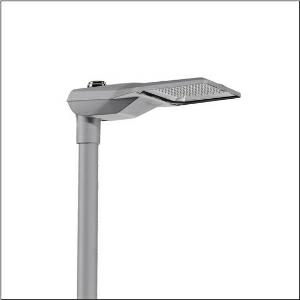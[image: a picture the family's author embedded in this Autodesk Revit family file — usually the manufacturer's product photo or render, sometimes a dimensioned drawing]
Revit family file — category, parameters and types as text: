
# Revit family: streetlight_sl_21_midi___st0_8a_5xe7c47n08lb_a78e
name_source: partatom
category: Lighting Fixtures
units: mm (PartAtom-declared; Revit-internal decimal feet)

## family parameters
Cut with Voids When Loaded = No
Host = Face
Light Source = No
Part Type = Normal
Room Calculation Point = No
Round Connector Dimension = Use Diameter
Shared = No

## types (1)
- --- (1 x LED, 14950 lm, 98.3 W, 4000K)
    Apparent Load = 98 VA
    CIE Flux Codes = 38 75 97 100 100
    Color Rendering = 70
    Color Temperature = 4000K
    Default Elevation = 1800 mm
    Description = Streetlight SL 21 midi, mast luminaire, primary light control with lens, of PMMA, primary optical cover: cover, of toughened safety glass, transparent, light distribution: ST0.8a, light emission: direct distribution, primary light characteristic: asymmetric, installation type: side-entry, LED, 3G 2.5mm², High Power LED, rated luminous flux: 14.950lm, luminous efficacy: 152lm/W, light colour: 740, colour temperature: 4000K, control gear: NEMA (7pin), control: overheat protection, pre-setting: linear dimming characteristic, constant luminous flux control, time-dependent luminous flux control, flexible luminous flux parameterisation, mains connection: 220..240V, AC, 50/60Hz, connection cable pre-assembled, cable length: 10,5m, wiring characteristics: H05VV-F, start of lifetime: 98W, end of service life: 101W, reduction: 45W, luminaire housing, of diecast aluminium (EN AC-44300), powder-coated, SITECO metallic grey (DB 702S), corrosivity category C5 high according to DIN EN ISO 12944, multi-level sealing system, sealing non-destructively replaceable, inclination adjustable: 0°, 5°, 10°, 15°, length: 644mm, width: 335mm, height: 110mm, spigot size: 42mm (side-entry), mounting height: 4..8m, protection rating (complete): IP66, insulation class (complete): insulation class I (protective earthing), certification: CE, ENEC, ENEC+, VDE, impact resistance: IK10, permissible operating ambient temperature for outdoor applications: -40..+50°C, standard-compliant lighting for roads and squares, packaging unit: 1 piece

Light Distribution: ST0.8a
    Height = 111 mm
    Lamp = 1 x LED
    Lamp Light Flux = 14950 lm
    Lamp Power = 98.3 W
    Lamp count = 1
    Length = 644 mm
    Luminous efficacy = 152 lm/W
    Manufacturer = Siteco
    ModVariant = No
    Model = 5XE7C47N08LB
    Number of Poles = 1
    OnlyDefault = Yes
    Power Factor = 1
    Product Name = Streetlight SL 21 midi | ST0.8a
    Product group = mast luminaire | pylon top
    ProductGroupID = 6100
    Protection Class = Protection class I
    Protection Degree = IP 66
    RLX_Detail_Level = 1
    RLX_Emergency_Light_Flux = 0 lm
    RLX_Emergency_Type = 0
    RLX_Emergency_Type_DB = No
    RlxData = <blob elided: 26773 chars, md5=28e63cbd>
    Socket = socket
    Standby Power = 0 W
    System Light Flux = 14950 lm
    System Power = 98 W
    Type Comments = factory setting: luminous flux: 100 % | dim-lin: 254 | 1020 mA
    Type Image = l_1294377.jpg
    URL = http://relux.com
    VarID = @adj_133525
    Voltage = 0 V
    Weight = 0.00 kg
    Width = 336 mm

## geometry (parser evidence)
native form markers: Blend x4, Sweep x11
no freeform markers — native parametric forms only
